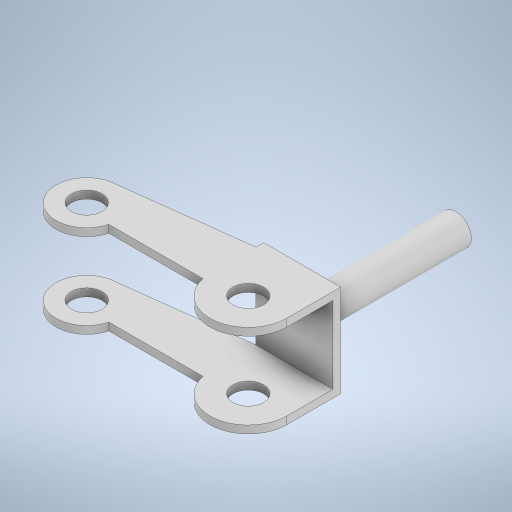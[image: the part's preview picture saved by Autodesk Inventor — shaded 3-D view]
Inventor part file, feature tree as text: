
AUTODESK INVENTOR PART (.ipt)
format: ipt  version: 2023.2 (Build 272271000, 271)  size: 348,672 bytes
history: native  units: mm
features: sketch x2, extrude x1
ambient origin geometry x8: Origin, YZ Plane, XZ Plane, XY Plane, X Axis, Y Axis, Z Axis, Center Point
bodies: Body1 (feature_tree)
feature tree (3):
  extrude  "Extrusion19"  Depth=10.0mm TaperAngle=0.0deg
  sketch  "Sketch2"  dims[d235=1.0mm d236=0.0mm d238=10.0mm d239=0.0mm]
  sketch  "Sketch4"  dims[d245=1.0mm d246=0.0mm d269=4.0mm d270=12.0mm d271=1.0mm d272=4.0mm d273=4.0mm d274=-1.0mm d275=-1.0mm d278=7.0mm d279=10.0mm d280=5.0mm d282=4.0mm d284=5.0mm d286=5.0mm d287=4.0mm d288=1.0mm d291=4.0mm d294=4.0mm d295=4.0mm d296=4.0mm d297=6.0mm d298=5.0mm d299=20.0mm d300=0.0mm d9=0.5mm d10=0.872665mm d11=0.5mm d12=0.872665mm d13=0.5mm d14=0.872665mm d27=0.5mm d28=0.872665mm d29=0.5mm d30=0.872665mm d88=0.5mm d89=0.872665mm d90=0.5mm d91=0.872665mm d116=0.5mm d117=0.872665mm d118=0.5mm d119=0.872665mm d154=0.5mm d155=0.872665mm d156=0.5mm d157=0.872665mm d181=0.5mm d182=0.872665mm d183=0.5mm d184=0.872665mm d221=0.5mm d222=0.872665mm d223=0.5mm d224=0.872665mm]
